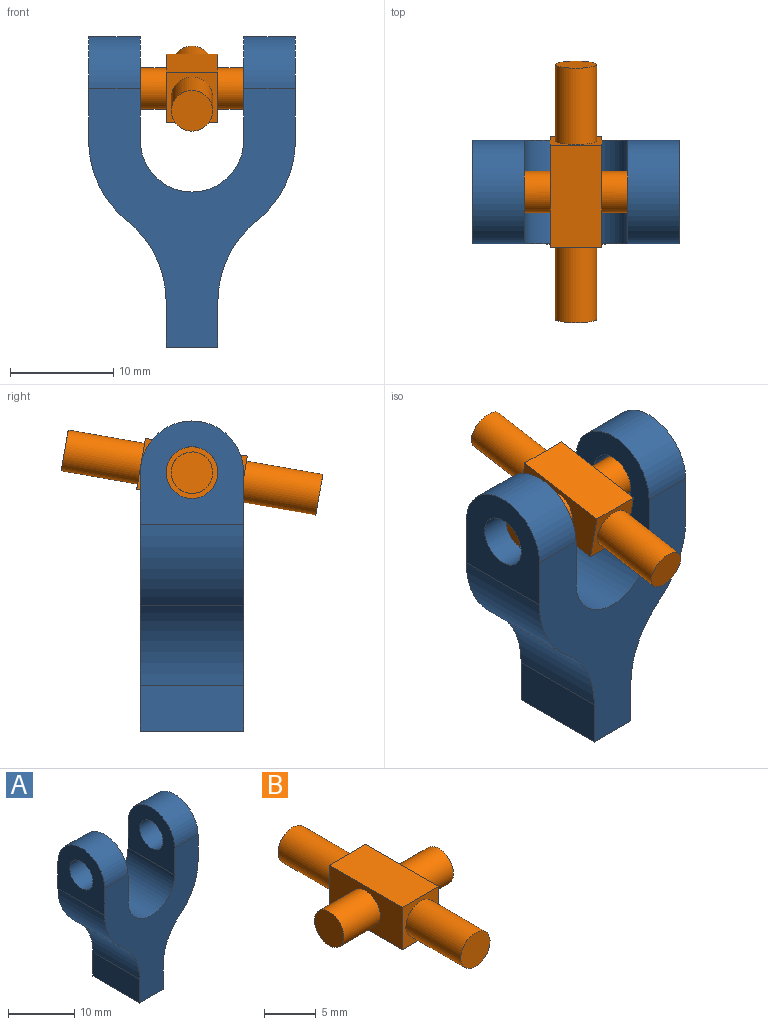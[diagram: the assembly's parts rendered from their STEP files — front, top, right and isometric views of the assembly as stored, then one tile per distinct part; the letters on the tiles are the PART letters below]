
ASSEMBLY  parts=2 mates=2
PART A: 18 faces, bbox 20x10x30 mm
  f0: plane 10x4.39mm, normal (-1,0,0), area 43.9mm2, adj f1,f11,f12,f13
  f1: plane 10x5mm, normal (0,0,-1), area 50mm2, adj f0,f2,f12,f13
  f2: plane 10x4.39mm, normal (1,0,0), area 43.9mm2, adj f1,f3,f12,f13
  f3: cylinder r=10mm len=10mm, axis (0,1,0), area 89.6mm2, adj f2,f4,f12,f13
  f4: cylinder r=10mm len=10mm, axis (0,1,0), area 89.6mm2, adj f3,f5,f12,f13
  f5: plane 10x10mm, normal (1,0,0), area 69.6mm2, adj f4,f12,f13,f15,f17
  f6: plane 10x10mm, normal (-1,0,0), area 69.6mm2, adj f7,f12,f13,f15,f17
  f7: cylinder r=5mm len=10mm, axis (0,1,0), area 157.1mm2, adj f6,f8,f12,f13
  f8: plane 10x10mm, normal (1,0,0), area 69.6mm2, adj f7,f12,f13,f14,f16
  f9: plane 10x10mm, normal (-1,0,0), area 69.6mm2, adj f10,f12,f13,f14,f16
  f10: cylinder r=10mm len=10mm, axis (0,1,0), area 89.6mm2, adj f9,f11,f12,f13
  f11: cylinder r=10mm len=10mm, axis (0,1,0), area 89.6mm2, adj f0,f10,f12,f13
  f12: plane 25x20mm, normal (0,-1,0), area 227.8mm2, adj f0,f1,f2,f3,f4,f5,f6,f7
  f13: plane 25x20mm, normal (0,1,0), area 227.8mm2, adj f0,f1,f2,f3,f4,f5,f6,f7
  f14: cylinder r=5mm len=10mm, axis (1,0,0), area 78.5mm2, adj f8,f9,f12,f13
  f15: cylinder r=5mm len=10mm, axis (1,0,0), area 78.5mm2, adj f5,f6,f12,f13
  f16: cylinder r=2.5mm len=5mm, axis (1,0,0), area 78.5mm2, adj f8,f9
  f17: cylinder r=2.5mm len=5mm, axis (1,0,0), area 78.5mm2, adj f5,f6
PART B: 14 faces, bbox 15x25x5 mm
  f0: plane 10x5mm, normal (1,0,0), area 37.4mm2, adj f1,f3,f4,f5,f12
  f1: plane 5x5mm, normal (0,1,0), area 12.4mm2, adj f0,f2,f4,f5,f8
  f2: plane 10x5mm, normal (-1,0,0), area 37.4mm2, adj f1,f3,f4,f5,f11
  f3: plane 5x5mm, normal (0,-1,0), area 12.4mm2, adj f0,f2,f4,f5,f7
  f4: plane 10x5mm, normal (0,0,1), area 50mm2, adj f0,f1,f2,f3
  f5: plane 10x5mm, normal (0,0,-1), area 50mm2, adj f0,f1,f2,f3
  f6: plane 4x4mm, normal (0,-1,0), area 12.6mm2, adj f7
  f7: cylinder r=2mm len=7.5mm, axis (0,1,0), area 94.2mm2, adj f3,f6
  f8: cylinder r=2mm len=7.5mm, axis (0,1,0), area 94.2mm2, adj f1,f9
  f9: plane 4x4mm, normal (0,1,0), area 12.6mm2, adj f8
  f10: plane 4x4mm, normal (-1,0,0), area 12.6mm2, adj f11
  f11: cylinder r=2mm len=5mm, axis (-1,0,0), area 62.8mm2, adj f2,f10
  f12: cylinder r=2mm len=5mm, axis (-1,0,0), area 62.8mm2, adj f0,f13
  f13: plane 4x4mm, normal (1,0,0), area 12.6mm2, adj f12
PLACE A at identity fixed
PLACE B rot(axis=(-1,0,0),170.1deg) t=(0,0,10)mm
MATE planar B.f11 <-> A.f14  axis (1,0,0) through (0,0,10)mm
MATE cylindrical B.f11 <-> A.f14  axis (-1,0,0) through (2.5,0,10)mm
